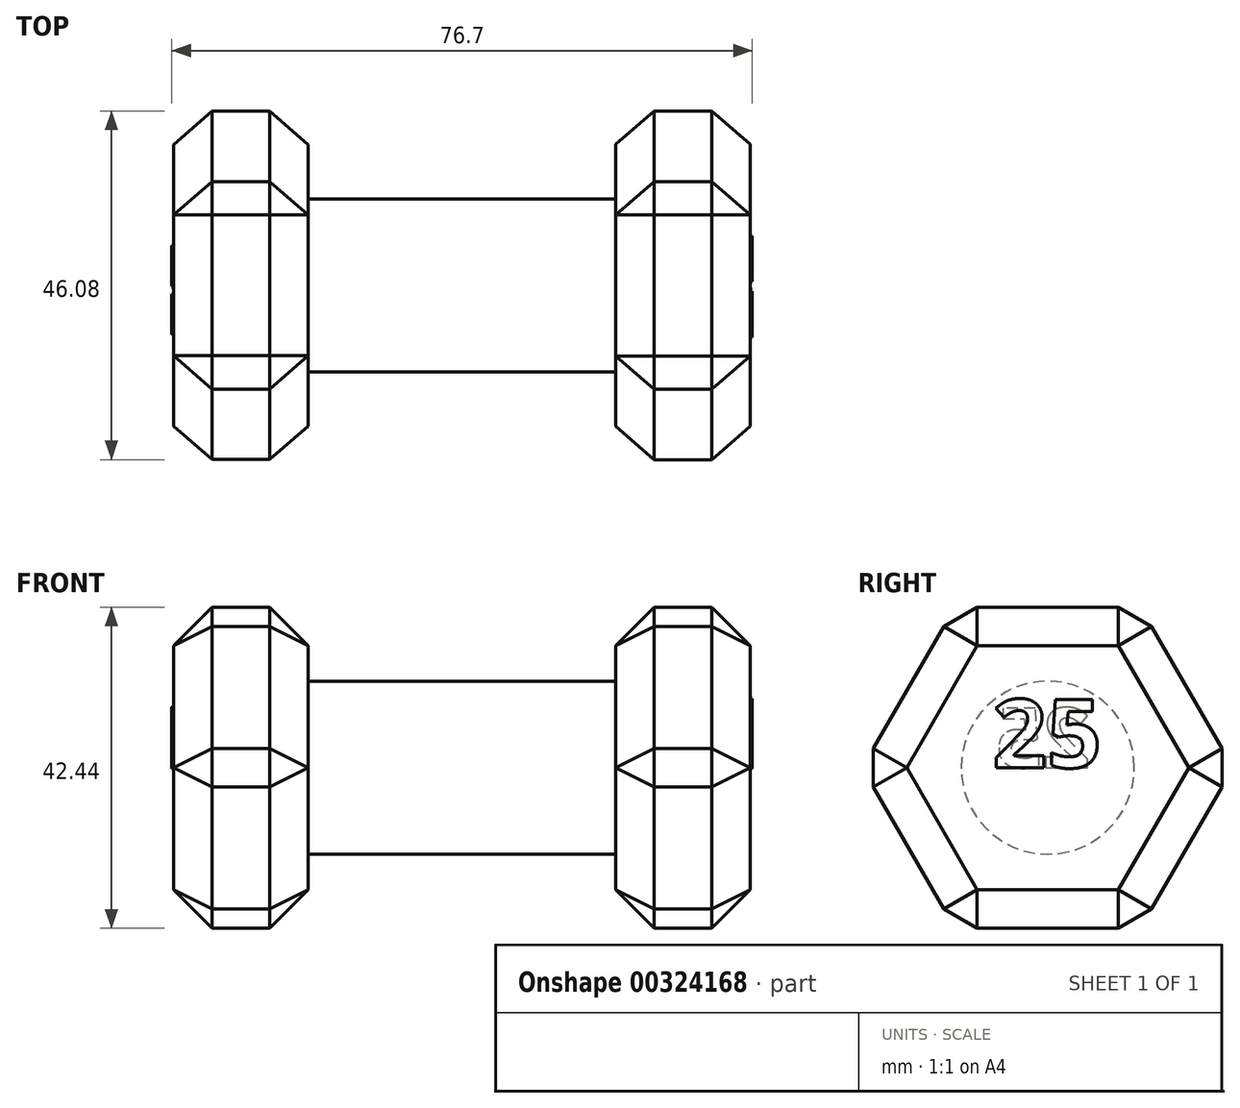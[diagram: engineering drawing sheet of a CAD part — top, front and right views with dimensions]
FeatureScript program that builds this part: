
annotation { "Feature Type Name" : "Feature", "Feature Type Description" : "" }
export const myFeature = defineFeature(function(context is Context, id is Id, definition is map)
    precondition{}
    {
        {
            var Q0;
            Q0=qCreatedBy(makeId("Right.planeOp"),FACE);
            var sketch = newSketch(context, id + "F0", { "sketchPlane" : qUnion([Q0])});
            skCircle(sketch, "E0.cCircle", {"center": v(0, 0) * mm, "radius": 21.2 * mm, "construction": true});
            skLineSegment(sketch, "E0.0", {"start": v(-12.24, 21.2) * mm, "end": v(12.24, 21.2) * mm});
            skLineSegment(sketch, "E0.1", {"start": v(12.24, 21.2) * mm, "end": v(24.48, 0) * mm});
            skLineSegment(sketch, "E0.2", {"start": v(24.48, 0) * mm, "end": v(12.24, -21.2) * mm});
            skLineSegment(sketch, "E0.3", {"start": v(12.24, -21.2) * mm, "end": v(-12.24, -21.2) * mm});
            skLineSegment(sketch, "E0.4", {"start": v(-12.24, -21.2) * mm, "end": v(-24.48, 0) * mm});
            skLineSegment(sketch, "E0.5", {"start": v(-24.48, 0) * mm, "end": v(-12.24, 21.2) * mm});
            skPoint(sketch, "E0.0.midPoint", {"position": v(0, 21.2) * mm});
            skCircle(sketch, "E1", {"center": v(0, 0) * mm, "radius": 11.43 * mm});
            skSolve(sketch);
        }
        {
            var Q0;
            Q0=makeQuery(id+"F0.imprint","IMPRINT",FACE,{"disambiguationData":[TD([[makeQuery(id+"F0.imprint","IMPRINT",EDGE,{"derivedFrom":sQuery(id+"F0.wireOp",EDGE,"E1")}),1.0]])]});
            extrude(context, id + "F1", {"entities" : qUnion([Q0]), "depth" : 76.2 * mm});
        }
        {
            var Q0;
            Q0 = qSketchRegion(id + "F0", true);
            extrude(context, id + "F2", {"entities" : qUnion([Q0]), "operationType" : NewBodyOperationType.ADD, "depth" : 17.78 * mm});
        }
        {
            var Q0;
            Q0=makeQuery(id+"F1.opExtrude","CAP_FACE",FACE,{"disambiguationData":[OSD([sQuery(id+"F0.wireOp",EDGE,"E1")])],"isStart":false});
            var sketch = newSketch(context, id + "F3", { "sketchPlane" : qUnion([Q0])});
            skCircle(sketch, "E2.cCircle", {"center": v(0, 0) * mm, "radius": 21.22 * mm, "construction": true});
            skLineSegment(sketch, "E2.0", {"start": v(-12.25, 21.22) * mm, "end": v(12.25, 21.22) * mm});
            skLineSegment(sketch, "E2.1", {"start": v(12.25, 21.22) * mm, "end": v(24.5, 0) * mm});
            skLineSegment(sketch, "E2.2", {"start": v(24.5, 0) * mm, "end": v(12.25, -21.22) * mm});
            skLineSegment(sketch, "E2.3", {"start": v(12.25, -21.22) * mm, "end": v(-12.25, -21.22) * mm});
            skLineSegment(sketch, "E2.4", {"start": v(-12.25, -21.22) * mm, "end": v(-24.5, 0) * mm});
            skLineSegment(sketch, "E2.5", {"start": v(-24.5, 0) * mm, "end": v(-12.25, 21.22) * mm});
            skPoint(sketch, "E2.0.midPoint", {"position": v(0, 21.22) * mm});
            skSolve(sketch);
        }
        {
            var Q0;
            Q0 = qSketchRegion(id + "F3", true);
            extrude(context, id + "F4", {"entities" : qUnion([Q0]), "operationType" : NewBodyOperationType.ADD, "oppositeDirection" : true, "depth" : 17.78 * mm});
        }
        {
            var Q0;
            Q0=makeQuery(id+"F2.opExtrude","CAP_EDGE",EDGE,{"disambiguationData":[OSD([sQuery(id+"F0.wireOp",EDGE,"E0.1")])],"isStart":true});
            var Q1;
            Q1=makeQuery(id+"F2.opExtrude","CAP_EDGE",EDGE,{"disambiguationData":[OSD([sQuery(id+"F0.wireOp",EDGE,"E0.0")])],"isStart":true});
            var Q2;
            Q2=makeQuery(id+"F2.opExtrude","CAP_EDGE",EDGE,{"disambiguationData":[OSD([sQuery(id+"F0.wireOp",EDGE,"E0.5")])],"isStart":true});
            var Q3;
            Q3=makeQuery(id+"F2.opExtrude","CAP_EDGE",EDGE,{"disambiguationData":[OSD([sQuery(id+"F0.wireOp",EDGE,"E0.5")])],"isStart":false});
            var Q4;
            Q4=makeQuery(id+"F2.opExtrude","SWEPT_EDGE",EDGE,{"disambiguationData":[OSD([sQuery(id+"F0.wireOp",EDGE,"E0.0"),sQuery(id+"F0.wireOp",EDGE,"E0.5")])]});
            var Q5;
            Q5=makeQuery(id+"F2.opExtrude","CAP_EDGE",EDGE,{"disambiguationData":[OSD([sQuery(id+"F0.wireOp",EDGE,"E0.0")])],"isStart":false});
            var Q6;
            Q6=makeQuery(id+"F2.opExtrude","SWEPT_EDGE",EDGE,{"disambiguationData":[OSD([sQuery(id+"F0.wireOp",EDGE,"E0.0"),sQuery(id+"F0.wireOp",EDGE,"E0.1")])]});
            var Q7;
            Q7=makeQuery(id+"F2.opExtrude","CAP_EDGE",EDGE,{"disambiguationData":[OSD([sQuery(id+"F0.wireOp",EDGE,"E0.1")])],"isStart":false});
            var Q8;
            Q8=makeQuery(id+"F2.opExtrude","SWEPT_EDGE",EDGE,{"disambiguationData":[OSD([sQuery(id+"F0.wireOp",EDGE,"E0.1"),sQuery(id+"F0.wireOp",EDGE,"E0.2")])]});
            var Q9;
            Q9=makeQuery(id+"F2.opExtrude","SWEPT_EDGE",EDGE,{"disambiguationData":[OSD([sQuery(id+"F0.wireOp",EDGE,"E0.4"),sQuery(id+"F0.wireOp",EDGE,"E0.5")])]});
            var Q10;
            Q10=makeQuery(id+"F2.opExtrude","SWEPT_EDGE",EDGE,{"disambiguationData":[OSD([sQuery(id+"F0.wireOp",EDGE,"E0.3"),sQuery(id+"F0.wireOp",EDGE,"E0.4")])]});
            var Q11;
            Q11=makeQuery(id+"F2.opExtrude","CAP_EDGE",EDGE,{"disambiguationData":[OSD([sQuery(id+"F0.wireOp",EDGE,"E0.3")])],"isStart":true});
            var Q12;
            Q12=makeQuery(id+"F2.opExtrude","CAP_EDGE",EDGE,{"disambiguationData":[OSD([sQuery(id+"F0.wireOp",EDGE,"E0.4")])],"isStart":true});
            var Q13;
            Q13=makeQuery(id+"F2.opExtrude","CAP_EDGE",EDGE,{"disambiguationData":[OSD([sQuery(id+"F0.wireOp",EDGE,"E0.4")])],"isStart":false});
            var Q14;
            Q14=makeQuery(id+"F2.opExtrude","CAP_EDGE",EDGE,{"disambiguationData":[OSD([sQuery(id+"F0.wireOp",EDGE,"E0.3")])],"isStart":false});
            var Q15;
            Q15=makeQuery(id+"F2.opExtrude","SWEPT_EDGE",EDGE,{"disambiguationData":[OSD([sQuery(id+"F0.wireOp",EDGE,"E0.2"),sQuery(id+"F0.wireOp",EDGE,"E0.3")])]});
            var Q16;
            Q16=makeQuery(id+"F2.opExtrude","CAP_EDGE",EDGE,{"disambiguationData":[OSD([sQuery(id+"F0.wireOp",EDGE,"E0.2")])],"isStart":true});
            var Q17;
            Q17=makeQuery(id+"F2.opExtrude","CAP_EDGE",EDGE,{"disambiguationData":[OSD([sQuery(id+"F0.wireOp",EDGE,"E0.2")])],"isStart":false});
            chamfer(context, id + "F5", {"entities" : qUnion([Q0, Q1, Q2, Q3, Q4, Q5, Q6, Q7, Q8, Q9, Q10, Q11, Q12, Q13, Q14, Q15, Q16, Q17]), "width" : 5.08 * mm, "tangentPropagation" : true});
        }
        {
            var Q0;
            Q0=makeQuery(id+"F4.opExtrude","CAP_EDGE",EDGE,{"disambiguationData":[OSD([sQuery(id+"F3.wireOp",EDGE,"E2.3")])],"isStart":false});
            var Q1;
            Q1=makeQuery(id+"F4.opExtrude","SWEPT_EDGE",EDGE,{"disambiguationData":[OSD([sQuery(id+"F3.wireOp",EDGE,"E2.3"),sQuery(id+"F3.wireOp",EDGE,"E2.4")])]});
            var Q2;
            Q2=makeQuery(id+"F4.opExtrude","SWEPT_EDGE",EDGE,{"disambiguationData":[OSD([sQuery(id+"F3.wireOp",EDGE,"E2.2"),sQuery(id+"F3.wireOp",EDGE,"E2.3")])]});
            var Q3;
            Q3=makeQuery(id+"F4.opExtrude","CAP_EDGE",EDGE,{"disambiguationData":[OSD([sQuery(id+"F3.wireOp",EDGE,"E2.2")])],"isStart":false});
            var Q4;
            Q4=makeQuery(id+"F4.opExtrude","CAP_EDGE",EDGE,{"disambiguationData":[OSD([sQuery(id+"F3.wireOp",EDGE,"E2.2")])],"isStart":true});
            var Q5;
            Q5=makeQuery(id+"F4.opExtrude","SWEPT_EDGE",EDGE,{"disambiguationData":[OSD([sQuery(id+"F3.wireOp",EDGE,"E2.1"),sQuery(id+"F3.wireOp",EDGE,"E2.2")])]});
            var Q6;
            Q6=makeQuery(id+"F4.opExtrude","CAP_EDGE",EDGE,{"disambiguationData":[OSD([sQuery(id+"F3.wireOp",EDGE,"E2.1")])],"isStart":false});
            var Q7;
            Q7=makeQuery(id+"F4.opExtrude","SWEPT_EDGE",EDGE,{"disambiguationData":[OSD([sQuery(id+"F3.wireOp",EDGE,"E2.0"),sQuery(id+"F3.wireOp",EDGE,"E2.1")])]});
            var Q8;
            Q8=makeQuery(id+"F4.opExtrude","CAP_EDGE",EDGE,{"disambiguationData":[OSD([sQuery(id+"F3.wireOp",EDGE,"E2.1")])],"isStart":true});
            var Q9;
            Q9=makeQuery(id+"F4.opExtrude","CAP_EDGE",EDGE,{"disambiguationData":[OSD([sQuery(id+"F3.wireOp",EDGE,"E2.3")])],"isStart":true});
            var Q10;
            Q10=makeQuery(id+"F4.opExtrude","CAP_EDGE",EDGE,{"disambiguationData":[OSD([sQuery(id+"F3.wireOp",EDGE,"E2.4")])],"isStart":false});
            var Q11;
            Q11=makeQuery(id+"F4.opExtrude","CAP_EDGE",EDGE,{"disambiguationData":[OSD([sQuery(id+"F3.wireOp",EDGE,"E2.4")])],"isStart":true});
            var Q12;
            Q12=makeQuery(id+"F4.opExtrude","CAP_EDGE",EDGE,{"disambiguationData":[OSD([sQuery(id+"F3.wireOp",EDGE,"E2.5")])],"isStart":true});
            var Q13;
            Q13=makeQuery(id+"F4.opExtrude","CAP_EDGE",EDGE,{"disambiguationData":[OSD([sQuery(id+"F3.wireOp",EDGE,"E2.5")])],"isStart":false});
            var Q14;
            Q14=makeQuery(id+"F4.opExtrude","SWEPT_EDGE",EDGE,{"disambiguationData":[OSD([sQuery(id+"F3.wireOp",EDGE,"E2.4"),sQuery(id+"F3.wireOp",EDGE,"E2.5")])]});
            var Q15;
            Q15=makeQuery(id+"F4.opExtrude","SWEPT_EDGE",EDGE,{"disambiguationData":[OSD([sQuery(id+"F3.wireOp",EDGE,"E2.0"),sQuery(id+"F3.wireOp",EDGE,"E2.5")])]});
            var Q16;
            Q16=makeQuery(id+"F4.opExtrude","CAP_EDGE",EDGE,{"disambiguationData":[OSD([sQuery(id+"F3.wireOp",EDGE,"E2.0")])],"isStart":false});
            var Q17;
            Q17=makeQuery(id+"F4.opExtrude","CAP_EDGE",EDGE,{"disambiguationData":[OSD([sQuery(id+"F3.wireOp",EDGE,"E2.0")])],"isStart":true});
            chamfer(context, id + "F6", {"entities" : qUnion([Q0, Q1, Q2, Q3, Q4, Q5, Q6, Q7, Q8, Q9, Q10, Q11, Q12, Q13, Q14, Q15, Q16, Q17]), "width" : 5.08 * mm, "tangentPropagation" : true});
        }
        {
            var Q0;
            Q0=makeQuery(id+"F4.boolean.opBoolean","MERGE",FACE,{"derivedFrom":[makeQuery(id+"F1.opExtrude","CAP_FACE",FACE,{"disambiguationData":[OSD([sQuery(id+"F0.wireOp",EDGE,"E1")])],"isStart":false}),makeQuery(id+"F4.opExtrude","CAP_FACE",FACE,{"disambiguationData":[OSD([sQuery(id+"F3.wireOp",EDGE,"E2.0"),sQuery(id+"F3.wireOp",EDGE,"E2.1"),sQuery(id+"F3.wireOp",EDGE,"E2.2"),sQuery(id+"F3.wireOp",EDGE,"E2.3"),sQuery(id+"F3.wireOp",EDGE,"E2.4"),sQuery(id+"F3.wireOp",EDGE,"E2.5")])],"isStart":true})]});
            var sketch = newSketch(context, id + "F7", { "sketchPlane" : qUnion([Q0])});
            skText(sketch, "E3", { "text": "25\n", "fontName": "OpenSans-Bold.ttf"});
            const initialGuessF7  = {"E3": [-0.00732, 0, 1, 0, 0.0091]};
            skSetInitialGuess(sketch, initialGuessF7);
            skSolve(sketch);
        }
        {
            var Q0;
            Q0 = qSketchRegion(id + "F7", true);
            extrude(context, id + "F8", {"entities" : qUnion([Q0]), "operationType" : NewBodyOperationType.ADD, "depth" : 0.25 * mm});
        }
        {
            var Q0;
            {var subQ0=sQuery(id+"F0.wireOp",EDGE,"E1");Q0=makeQuery(id+"F2.boolean.opBoolean","MERGE",FACE,{"derivedFrom":[makeQuery(id+"F1.opExtrude","CAP_FACE",FACE,{"disambiguationData":[OSD([subQ0])],"isStart":true}),makeQuery(id+"F2.opExtrude","CAP_FACE",FACE,{"disambiguationData":[OSD([sQuery(id+"F0.wireOp",EDGE,"E0.0"),sQuery(id+"F0.wireOp",EDGE,"E0.1"),sQuery(id+"F0.wireOp",EDGE,"E0.2"),sQuery(id+"F0.wireOp",EDGE,"E0.3"),sQuery(id+"F0.wireOp",EDGE,"E0.4"),sQuery(id+"F0.wireOp",EDGE,"E0.5"),subQ0])],"isStart":true})]});}
            var sketch = newSketch(context, id + "F9", { "sketchPlane" : qUnion([Q0])});
            skText(sketch, "E4", { "text": "25\n", "fontName": "OpenSans-Bold.ttf"});
            const initialGuessF9  = {"E4": [-0.00567, 0, 1, 0, 0.00796]};
            skSetInitialGuess(sketch, initialGuessF9);
            skSolve(sketch);
        }
        {
            var Q0;
            Q0 = qSketchRegion(id + "F9", true);
            extrude(context, id + "F10", {"entities" : qUnion([Q0]), "operationType" : NewBodyOperationType.ADD, "depth" : 0.25 * mm});
        }
    });
